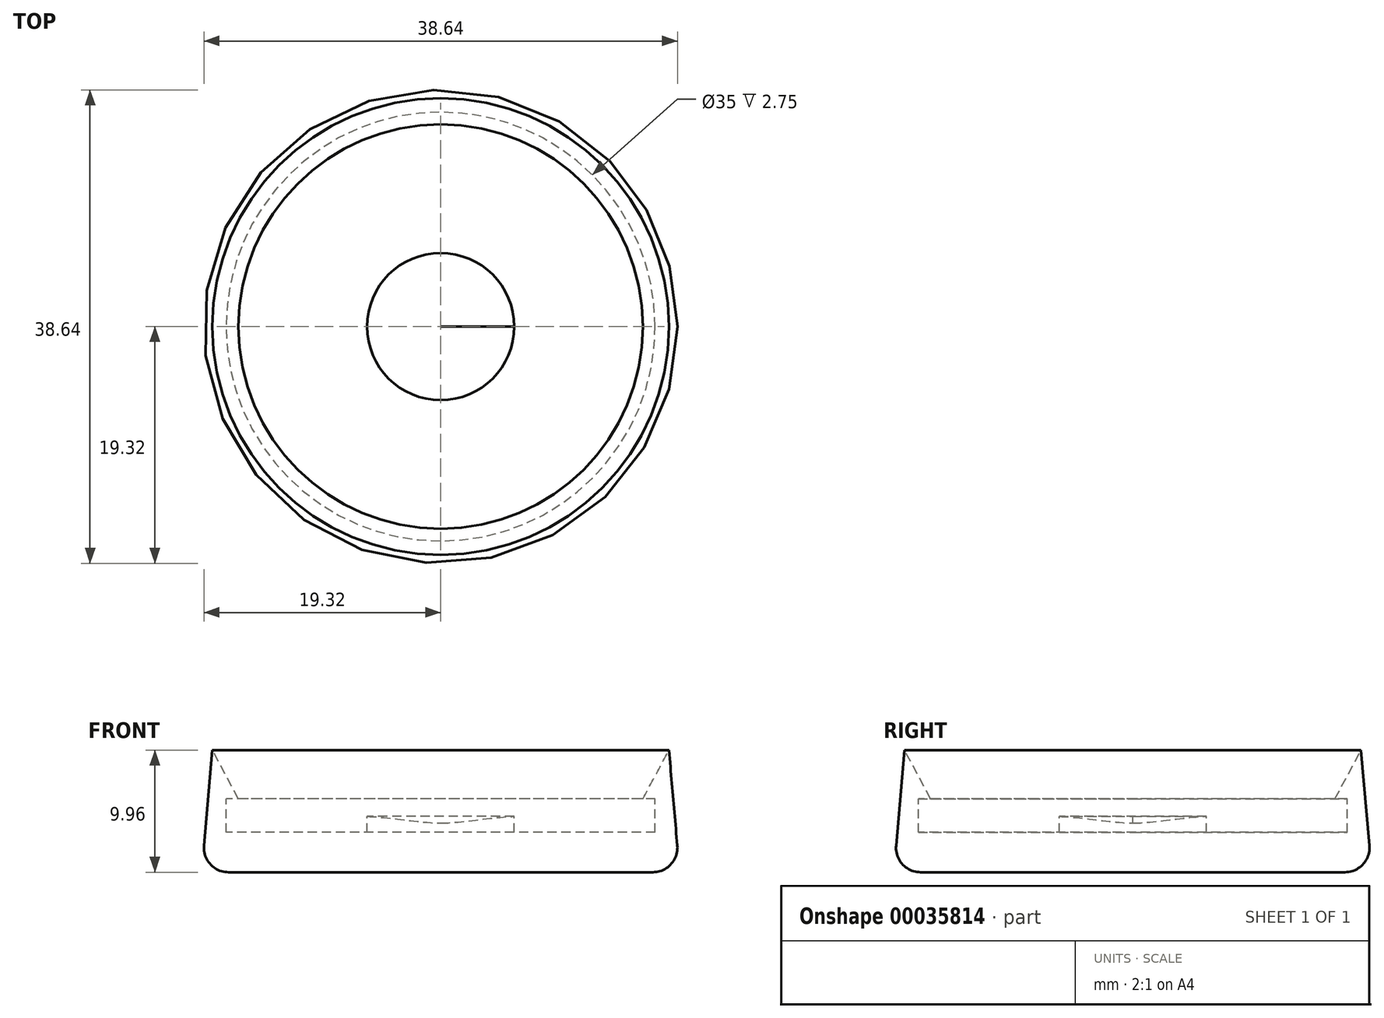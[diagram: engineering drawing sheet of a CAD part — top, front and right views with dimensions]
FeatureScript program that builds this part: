
annotation { "Feature Type Name" : "Feature", "Feature Type Description" : "" }
export const myFeature = defineFeature(function(context is Context, id is Id, definition is map)
    precondition{}
    {
        {
            var Q0;
            Q0=qCreatedBy(makeId("Front.planeOp"),FACE);
            var sketch = newSketch(context, id + "F0", { "sketchPlane" : qUnion([Q0])});
            skLineSegment(sketch, "E0", {"start": v(0, 0) * mm, "end": v(19.5, 0) * mm});
            skLineSegment(sketch, "E1", {"start": v(19.5, 0) * mm, "end": v(18.63, 9.96) * mm});
            skLineSegment(sketch, "E2", {"start": v(18.63, 9.96) * mm, "end": v(16.5, 6) * mm});
            skLineSegment(sketch, "E3", {"start": v(16.5, 6) * mm, "end": v(17.5, 6) * mm});
            skLineSegment(sketch, "E4", {"start": v(17.5, 6) * mm, "end": v(17.5, 3.25) * mm});
            skLineSegment(sketch, "E5", {"start": v(17.5, 3.25) * mm, "end": v(0, 3.25) * mm});
            skLineSegment(sketch, "E6", {"start": v(0, 3.25) * mm, "end": v(0, 0) * mm});
            skLineSegment(sketch, "E7.left", {"start": v(0, 3.25) * mm, "end": v(0, 4) * mm});
            skLineSegment(sketch, "E7.right", {"start": v(6, 3.25) * mm, "end": v(6, 4.54) * mm});
            skFitSpline(sketch, "E8", {"points": [v(0, 4) * mm, v(6, 4.54) * mm], "startDerivative": vector(4.38, 0) * mm, "endDerivative": vector(4.38, 0) * mm});
            skSolve(sketch);
        }
        {
            var Q0;
            Q0 = qSketchRegion(id + "F0", true);
            var Q1;
            Q1=sQuery(id+"F0.wireOp",EDGE,"E6");
            revolve(context, id + "F1", {"entities" : qUnion([Q0]), "axis" : qUnion([Q1]), "revolveType" : RevolveType.FULL});
        }
        {
            var Q0;
            Q0=makeQuery(id+"F1.opRevolve","SWEPT_EDGE",EDGE,{"disambiguationData":[OSD([sQuery(id+"F0.wireOp",EDGE,"E0"),sQuery(id+"F0.wireOp",EDGE,"E1")])]});
            fillet(context, id + "F2", {"entities" : qUnion([Q0]), "radius" : 2 * mm, "tangentPropagation" : true, "allowEdgeOverflow" : false});
        }
    });
